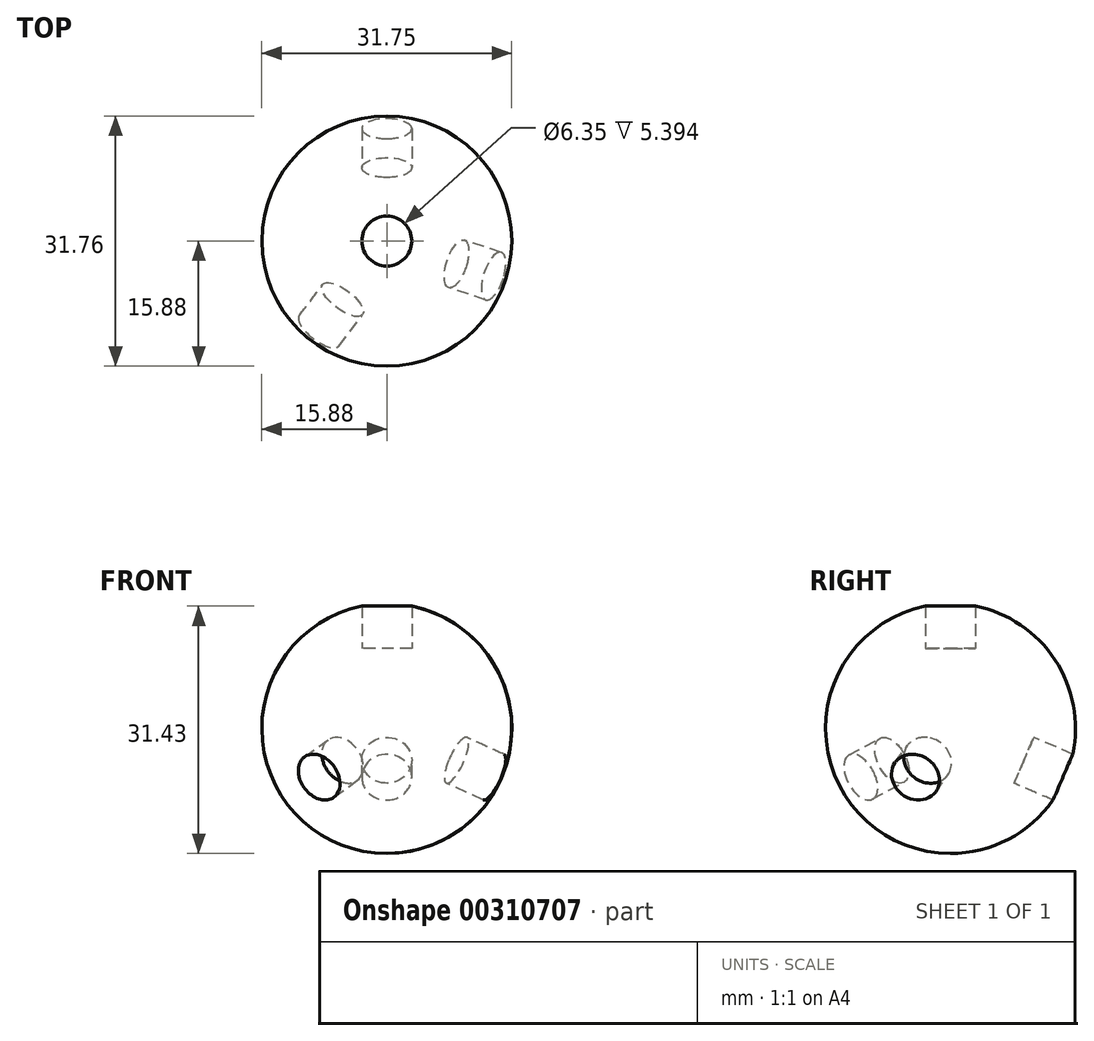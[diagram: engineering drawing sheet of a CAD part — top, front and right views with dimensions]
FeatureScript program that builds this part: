
annotation { "Feature Type Name" : "Feature", "Feature Type Description" : "" }
export const myFeature = defineFeature(function(context is Context, id is Id, definition is map)
    precondition{}
    {
        {
            var Q0;
            Q0=qCreatedBy(makeId("Front.planeOp"),FACE);
            var sketch = newSketch(context, id + "F0", { "sketchPlane" : qUnion([Q0])});
            skArc(sketch, "E0", {"start": v(0, 15.88) * mm, "mid": v(-15.88, 0) * mm, "end": v(0, -15.88) * mm});
            skLineSegment(sketch, "E1", {"start": v(0, 15.88) * mm, "end": v(0, -15.88) * mm});
            skSolve(sketch);
        }
        {
            var Q0;
            Q0=qCreatedBy(makeId("Top.planeOp"),FACE);
            var sketch = newSketch(context, id + "F1", { "sketchPlane" : qUnion([Q0])});
            skCircle(sketch, "E2", {"center": v(0, 0) * mm, "radius": 15.88 * mm});
            skSolve(sketch);
        }
        {
            var Q0;
            Q0=makeQuery(id+"F0.imprint","IMPRINT",FACE,{"disambiguationData":[TD([[makeQuery(id+"F0.imprint","IMPRINT",EDGE,{"derivedFrom":sQuery(id+"F0.wireOp",EDGE,"E0")}),1.0]])]});
            var Q1;
            Q1=sQuery(id+"F1.wireOp",EDGE,"E2");
            revolve(context, id + "F2", {"entities" : qUnion([Q0]), "axis" : qUnion([Q1]), "revolveType" : RevolveType.FULL});
        }
        {
            var Q0;
            Q0=qCreatedBy(makeId("Top.planeOp"),FACE);
            cPlane(context, id + "F3", {"entities" : qUnion([Q0]), "cplaneType" : CPlaneType.OFFSET, "offset" : 10.16 * mm, "width" : 152.4 * mm, "height" : 152.4 * mm});
        }
        {
            var Q0;
            Q0=qCreatedBy(id+"F3.planeOp",FACE);
            var sketch = newSketch(context, id + "F4", { "sketchPlane" : qUnion([Q0])});
            skCircle(sketch, "E3", {"center": v(0, 0) * mm, "radius": 3.18 * mm});
            skSolve(sketch);
        }
        {
            var Q0;
            Q0=qSketchRegion(id+"F4",true);
            extrude(context, id + "F5", {"entities" : qUnion([Q0]), "depth" : 50.8 * mm});
        }
        {
            var Q0;
            Q0=qCreatedBy(makeId("Front.planeOp"),FACE);
            var sketch = newSketch(context, id + "F6", { "sketchPlane" : qUnion([Q0])});
            skLineSegment(sketch, "E4", {"start": v(0, 0) * mm, "end": v(0, -58.07) * mm, "construction": true});
            skLineSegment(sketch, "E5", {"start": v(0, 0) * mm, "end": v(-72.63, 0) * mm, "construction": true});
            skSolve(sketch);
        }
        {
            var Q0;
            Q0=makeQuery(id+"F5.opExtrude","SWEPT_BODY",BODY,{"disambiguationData":[OSD([sQuery(id+"F4.wireOp",EDGE,"E3")])]});
            var Q1;
            Q1=sQuery(id+"F6.wireOp",EDGE,"E5");
            transform(context, id + "F7", {"entities" : qUnion([Q0]), "transformType" : TransformType.ROTATION, "transformAxis" : qUnion([Q1]), "angle" : 113.4 * degree, "makeCopy" : true});
        }
        {
            var Q0;
            Q0=makeQuery(id+"F7.opPattern","COPY",BODY,{"derivedFrom":makeQuery(id+"F5.opExtrude","SWEPT_BODY",BODY,{"disambiguationData":[OSD([sQuery(id+"F4.wireOp",EDGE,"E3")])]}),"instanceName":"1"});
            var Q1;
            Q1=sQuery(id+"F6.wireOp",EDGE,"E4");
            transform(context, id + "F8", {"entities" : qUnion([Q0]), "transformType" : TransformType.ROTATION, "transformAxis" : qUnion([Q1]), "angle" : 108.2 * degree, "makeCopy" : true});
        }
        {
            var Q0;
            Q0=makeQuery(id+"F8.opPattern","COPY",BODY,{"derivedFrom":makeQuery(id+"F7.opPattern","COPY",BODY,{"derivedFrom":makeQuery(id+"F5.opExtrude","SWEPT_BODY",BODY,{"disambiguationData":[OSD([sQuery(id+"F4.wireOp",EDGE,"E3")])]}),"instanceName":"1"}),"instanceName":"1"});
            var Q1;
            Q1=sQuery(id+"F6.wireOp",EDGE,"E4");
            transform(context, id + "F9", {"entities" : qUnion([Q0]), "transformType" : TransformType.ROTATION, "transformAxis" : qUnion([Q1]), "angle" : 108.8 * degree, "makeCopy" : true});
        }
        {
            var Q0;
            Q0=makeQuery(id+"F5.opExtrude","SWEPT_BODY",BODY,{"disambiguationData":[OSD([sQuery(id+"F4.wireOp",EDGE,"E3")])]});
            var Q1;
            Q1=makeQuery(id+"F7.opPattern","COPY",BODY,{"derivedFrom":makeQuery(id+"F5.opExtrude","SWEPT_BODY",BODY,{"disambiguationData":[OSD([sQuery(id+"F4.wireOp",EDGE,"E3")])]}),"instanceName":"1"});
            var Q2;
            Q2=makeQuery(id+"F9.opPattern","COPY",BODY,{"derivedFrom":makeQuery(id+"F8.opPattern","COPY",BODY,{"derivedFrom":makeQuery(id+"F7.opPattern","COPY",BODY,{"derivedFrom":makeQuery(id+"F5.opExtrude","SWEPT_BODY",BODY,{"disambiguationData":[OSD([sQuery(id+"F4.wireOp",EDGE,"E3")])]}),"instanceName":"1"}),"instanceName":"1"}),"instanceName":"1"});
            var Q3;
            Q3=makeQuery(id+"F8.opPattern","COPY",BODY,{"derivedFrom":makeQuery(id+"F7.opPattern","COPY",BODY,{"derivedFrom":makeQuery(id+"F5.opExtrude","SWEPT_BODY",BODY,{"disambiguationData":[OSD([sQuery(id+"F4.wireOp",EDGE,"E3")])]}),"instanceName":"1"}),"instanceName":"1"});
            var Q4;
            Q4=makeQuery(id+"F2.opRevolve","SWEPT_BODY",BODY,{"disambiguationData":[OSD([sQuery(id+"F0.wireOp",EDGE,"E0"),sQuery(id+"F0.wireOp",EDGE,"E1")])]});
            booleanBodies(context, id + "F10", {"operationType" : BooleanOperationType.SUBTRACTION, "tools" : qUnion([Q0, Q1, Q2, Q3]), "targets" : qUnion([Q4])});
        }
    });
